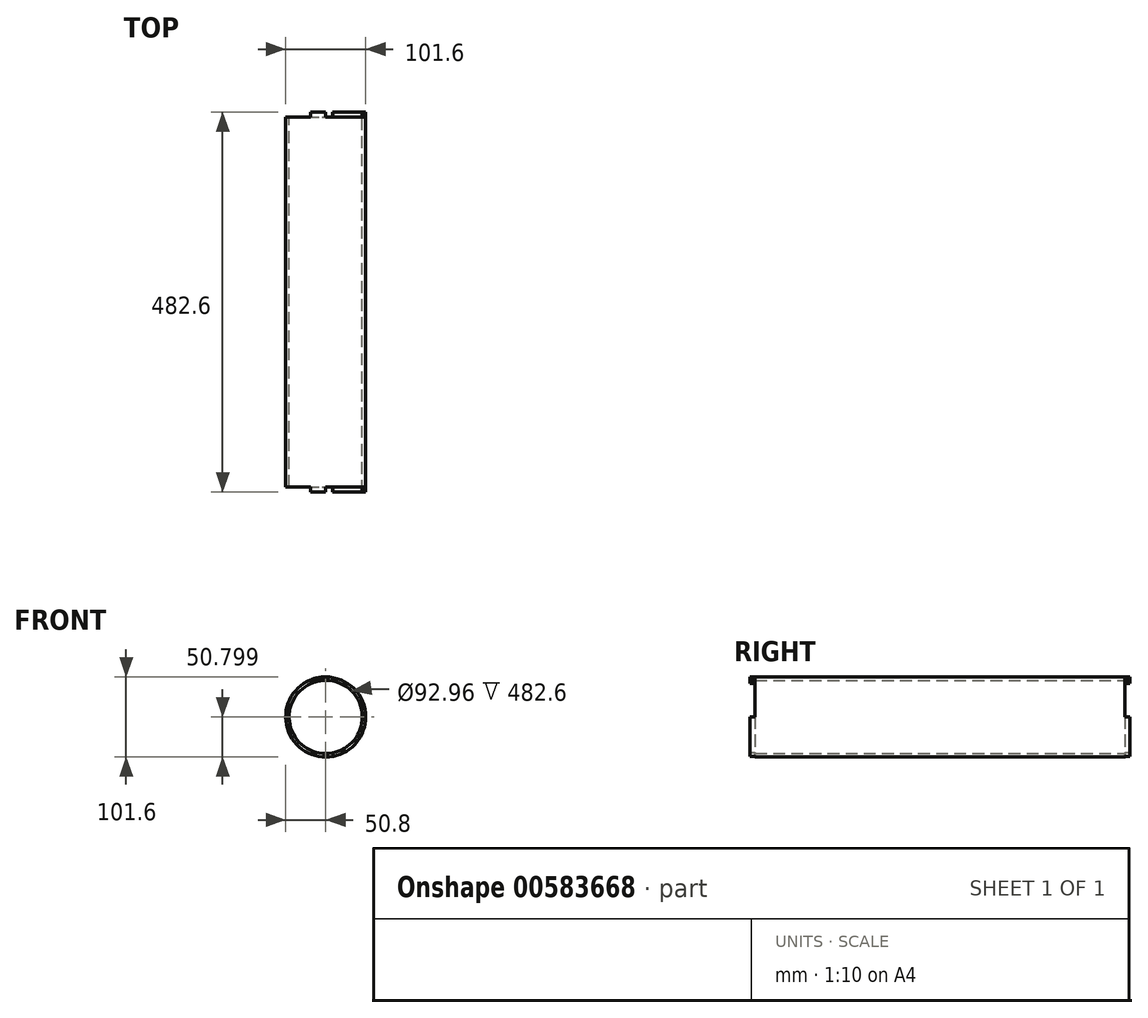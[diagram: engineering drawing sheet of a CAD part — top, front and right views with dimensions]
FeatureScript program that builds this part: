
annotation { "Feature Type Name" : "Feature", "Feature Type Description" : "" }
export const myFeature = defineFeature(function(context is Context, id is Id, definition is map)
    precondition{}
    {
        {
            var Q0;
            Q0=qCreatedBy(makeId("Front.planeOp"),FACE);
            var sketch = newSketch(context, id + "F0", { "sketchPlane" : qUnion([Q0])});
            skCircle(sketch, "E0", {"center": v(0, -0.08) * mm, "radius": 46.48 * mm});
            skCircle(sketch, "E1", {"center": v(0, -0.08) * mm, "radius": 50.8 * mm});
            skLineSegment(sketch, "E2", {"start": v(0, 50.72) * mm, "end": v(0, 46.4) * mm});
            skLineSegment(sketch, "E3", {"start": v(0, 46.4) * mm, "end": v(-18.65, 42.5) * mm});
            skLineSegment(sketch, "E4", {"start": v(-18.65, 42.5) * mm, "end": v(-19.55, 46.8) * mm});
            skSolve(sketch);
        }
        {
            var Q0;
            {var subQ1=sQuery(id+"F0.wireOp",EDGE,"E2");Q0=makeQuery(id+"F0.imprint","IMPRINT",FACE,{"disambiguationData":[TD([[makeQuery(id+"F0.imprint","IMPRINT",EDGE,{"derivedFrom":subQ1}),1.0]])]});}
            var Q1;
            {var subQ1=sQuery(id+"F0.wireOp",EDGE,"E2");Q1=makeQuery(id+"F0.imprint","IMPRINT",FACE,{"disambiguationData":[TD([[makeQuery(id+"F0.imprint","IMPRINT",EDGE,{"derivedFrom":subQ1}),-1.0]])]});}
            extrude(context, id + "F1", {"entities" : qUnion([Q0, Q1]), "depth" : 469.9 * mm, "offsetDistance" : 25.4 * mm});
        }
        {
            var Q0;
            Q0=makeQuery(id+"F1.opExtrude","CAP_FACE",FACE,{"disambiguationData":[OSD([sQuery(id+"F0.wireOp",EDGE,"E0"),sQuery(id+"F0.wireOp",EDGE,"E1")])],"isStart":true});
            var sketch = newSketch(context, id + "F2", { "sketchPlane" : qUnion([Q0])});
            skLineSegment(sketch, "E5", {"start": v(0, 50.72) * mm, "end": v(0, 46.4) * mm});
            skLineSegment(sketch, "E6", {"start": v(0, 46.4) * mm, "end": v(18.65, 42.5) * mm});
            skLineSegment(sketch, "E7", {"start": v(18.65, 42.5) * mm, "end": v(19.55, 46.8) * mm});
            skLineSegment(sketch, "E8", {"start": v(-46.48, 0) * mm, "end": v(-50.8, 0) * mm});
            skLineSegment(sketch, "E9", {"start": v(-9.7, -49.94) * mm, "end": v(-8.88, -45.7) * mm});
            skSolve(sketch);
        }
        {
            var Q0;
            Q0 = qSketchRegion(id + "F2", true);
            var Q1;
            {var subQ0=sQuery(id+"F2.wireOp",EDGE,"E5");Q1=makeQuery(id+"F2.imprint","IMPRINT",FACE,{"disambiguationData":[TD([[makeQuery(id+"F2.imprint","IMPRINT",EDGE,{"derivedFrom":subQ0}),1.0]])]});}
            var Q2;
            {var subQ0=sQuery(id+"F2.wireOp",EDGE,"E8");Q2=makeQuery(id+"F2.imprint","IMPRINT",FACE,{"disambiguationData":[TD([[makeQuery(id+"F2.imprint","IMPRINT",EDGE,{"derivedFrom":subQ0}),1.0]])]});}
            extrude(context, id + "F3", {"entities" : qUnion([Q0, Q1, Q2]), "operationType" : NewBodyOperationType.ADD, "depth" : 6.35 * mm, "offsetDistance" : 25.4 * mm, "hasSecondDirection" : true, "secondDirectionOppositeDirection" : true, "secondDirectionDepth" : 476.25 * mm});
        }
    });
